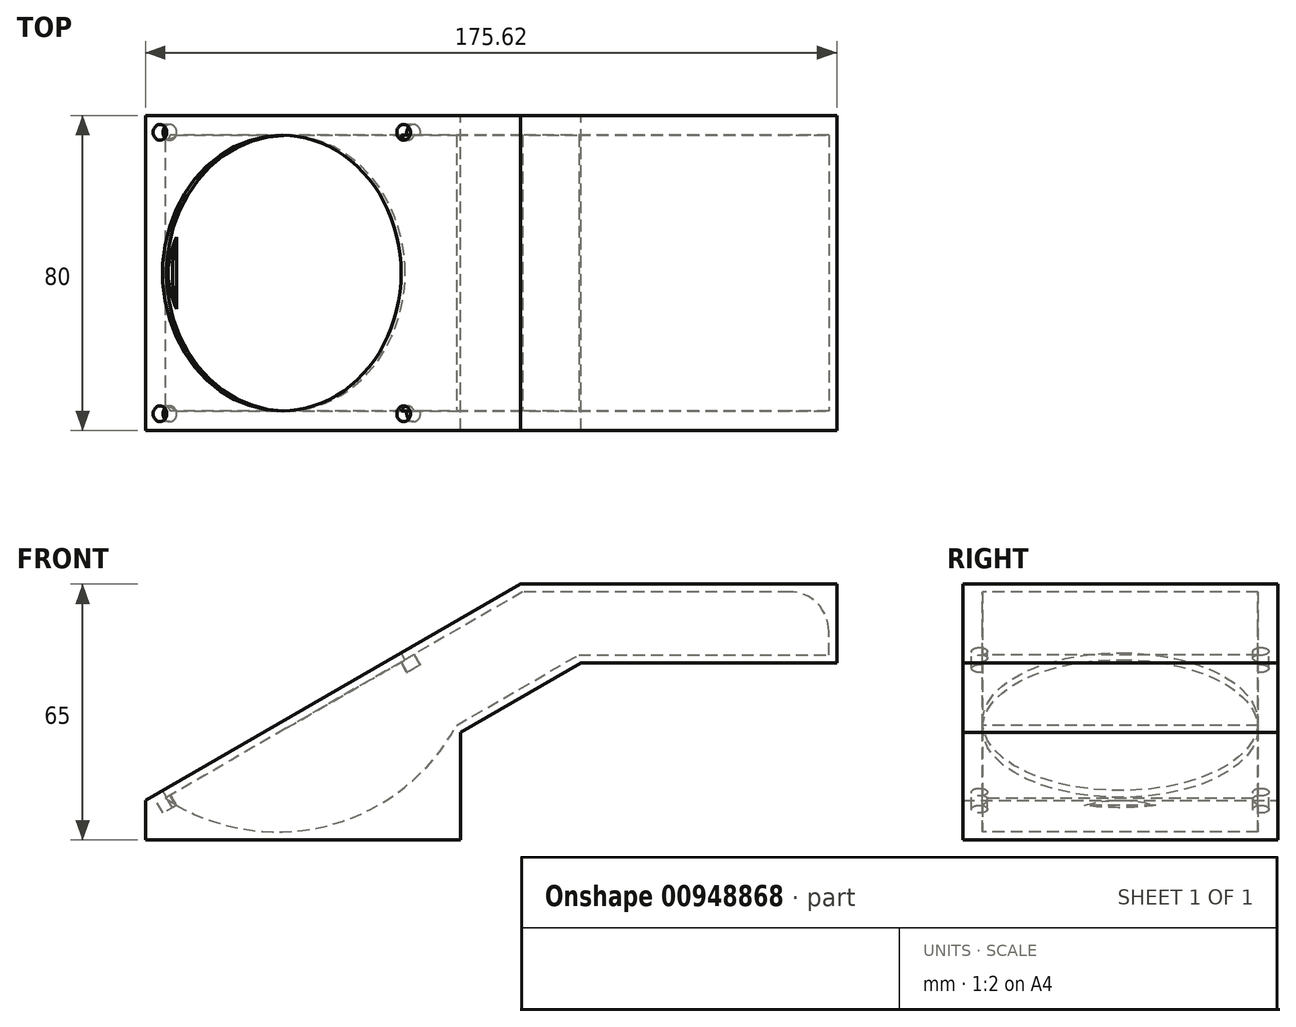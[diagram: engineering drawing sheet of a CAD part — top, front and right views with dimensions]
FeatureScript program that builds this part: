
annotation { "Feature Type Name" : "Feature", "Feature Type Description" : "" }
export const myFeature = defineFeature(function(context is Context, id is Id, definition is map)
    precondition{}
    {
        {
            var Q0;
            Q0=qCreatedBy(makeId("Front.planeOp"),FACE);
            var sketch = newSketch(context, id + "F0", { "sketchPlane" : qUnion([Q0])});
            skLineSegment(sketch, "E0.bottom", {"start": v(40.9, 9.17) * mm, "end": v(-28.4, -30.83) * mm});
            skLineSegment(sketch, "E0.top", {"start": v(28.4, 30.83) * mm, "end": v(-40.9, -9.17) * mm});
            skLineSegment(sketch, "E0.left", {"start": v(40.9, 9.17) * mm, "end": v(28.4, 30.83) * mm});
            skLineSegment(sketch, "E0.right", {"start": v(-28.4, -30.83) * mm, "end": v(-40.9, -9.17) * mm});
            skPoint(sketch, "E0.middle", {"position": v(0, 0) * mm});
            skLineSegment(sketch, "E1", {"start": v(0, 0) * mm, "end": v(56.66, 0) * mm, "construction": true});
            skLineSegment(sketch, "E2", {"start": v(-28.4, -40.83) * mm, "end": v(51.6, -40.83) * mm});
            skLineSegment(sketch, "E3", {"start": v(-28.4, -30.83) * mm, "end": v(-28.4, -40.83) * mm});
            skLineSegment(sketch, "E4", {"start": v(82.23, 4.17) * mm, "end": v(147.23, 4.17) * mm});
            skLineSegment(sketch, "E5", {"start": v(40.9, 9.17) * mm, "end": v(66.87, 24.17) * mm});
            skLineSegment(sketch, "E6", {"start": v(66.87, 24.17) * mm, "end": v(147.23, 24.17) * mm});
            skLineSegment(sketch, "E7", {"start": v(147.23, 4.17) * mm, "end": v(147.23, 24.17) * mm});
            skLineSegment(sketch, "E8", {"start": v(51.6, -40.83) * mm, "end": v(51.6, -13.5) * mm});
            skLineSegment(sketch, "E9", {"start": v(51.6, -13.5) * mm, "end": v(82.23, 4.17) * mm});
            skSolve(sketch);
        }
        {
            var Q0;
            Q0=makeQuery(id+"F0.imprint","IMPRINT",FACE,{"disambiguationData":[TD([[makeQuery(id+"F0.imprint","IMPRINT",EDGE,{"derivedFrom":sQuery(id+"F0.wireOp",EDGE,"E0.bottom")}),1.0]])]});
            extrude(context, id + "F1", {"entities" : qUnion([Q0]), "endBound" : BoundingType.SYMMETRIC, "depth" : 80 * mm, "offsetDistance" : 25 * mm});
        }
        {
            var Q0;
            Q0=qCreatedBy(makeId("Front.planeOp"),FACE);
            var sketch = newSketch(context, id + "F2", { "sketchPlane" : qUnion([Q0])});
            skLineSegment(sketch, "E10", {"start": v(50.6, -11.77) * mm, "end": v(81.7, 6.17) * mm});
            skLineSegment(sketch, "E11", {"start": v(81.7, 6.17) * mm, "end": v(145.23, 6.17) * mm});
            skLineSegment(sketch, "E12", {"start": v(145.23, 6.17) * mm, "end": v(145.23, 12.17) * mm});
            skLineSegment(sketch, "E13", {"start": v(135.23, 22.17) * mm, "end": v(67.4, 22.17) * mm});
            skLineSegment(sketch, "E14", {"start": v(67.4, 22.17) * mm, "end": v(-23.42, -30.27) * mm});
            skArc(sketch, "E15", {"start": v(-23.42, -30.27) * mm, "mid": v(17.66, -37.28) * mm, "end": v(50.6, -11.77) * mm});
            skPoint(sketch, "E16.visualSharp", {"position": v(145.23, 22.17) * mm});
            skArc(sketch, "E16.filletArc", {"start": v(145.23, 12.17) * mm, "mid": v(142.3, 19.25) * mm, "end": v(135.23, 22.17) * mm});
            skSolve(sketch);
        }
        {
            var Q0;
            Q0 = qSketchRegion(id + "F2", true);
            extrude(context, id + "F3", {"entities" : qUnion([Q0]), "operationType" : NewBodyOperationType.REMOVE, "endBound" : BoundingType.SYMMETRIC, "oppositeDirection" : true, "depth" : 70 * mm, "offsetDistance" : 25 * mm});
        }
        {
            var Q0;
            Q0=makeQuery(id+"F1.opExtrude","SWEPT_FACE",FACE,{"disambiguationData":[OSD([sQuery(id+"F0.wireOp",EDGE,"E0.bottom"),sQuery(id+"F0.wireOp",EDGE,"E5")])]});
            var sketch = newSketch(context, id + "F4", { "sketchPlane" : qUnion([Q0])});
            skLineSegment(sketch, "E17.bottom", {"start": v(-40, 40) * mm, "end": v(40, 40) * mm, "construction": true});
            skLineSegment(sketch, "E17.top", {"start": v(-40, -40) * mm, "end": v(40, -40) * mm, "construction": true});
            skLineSegment(sketch, "E17.left", {"start": v(-40, 40) * mm, "end": v(-40, -40) * mm, "construction": true});
            skLineSegment(sketch, "E17.right", {"start": v(40, 40) * mm, "end": v(40, -40) * mm, "construction": true});
            skLineSegment(sketch, "E18", {"start": v(-40, 40) * mm, "end": v(40, -40) * mm, "construction": true});
            skCircle(sketch, "E19", {"center": v(0, 0) * mm, "radius": 35 * mm});
            skLineSegment(sketch, "E20.bottom", {"start": v(35.75, -35.75) * mm, "end": v(-35.75, -35.75) * mm, "construction": true});
            skLineSegment(sketch, "E20.top", {"start": v(35.75, 35.75) * mm, "end": v(-35.75, 35.75) * mm, "construction": true});
            skLineSegment(sketch, "E20.left", {"start": v(35.75, -35.75) * mm, "end": v(35.75, 35.75) * mm, "construction": true});
            skLineSegment(sketch, "E20.right", {"start": v(-35.75, -35.75) * mm, "end": v(-35.75, 35.75) * mm, "construction": true});
            skCircle(sketch, "E21", {"center": v(-35.75, 35.75) * mm, "radius": 2 * mm});
            skCircle(sketch, "E22", {"center": v(35.75, 35.75) * mm, "radius": 2 * mm});
            skCircle(sketch, "E23", {"center": v(35.75, -35.75) * mm, "radius": 2 * mm});
            skCircle(sketch, "E24", {"center": v(-35.75, -35.75) * mm, "radius": 2 * mm});
            skSolve(sketch);
        }
        {
            var Q0;
            Q0 = qSketchRegion(id + "F4", true);
            extrude(context, id + "F5", {"entities" : qUnion([Q0]), "operationType" : NewBodyOperationType.REMOVE, "oppositeDirection" : true, "depth" : 5 * mm, "offsetDistance" : 25 * mm});
        }
    });
